# Revit family: 1f8d478efd5c45ef9d9ec268079f8082
name_source: partatom
category: Portes
units: mm (PartAtom-declared; Revit-internal decimal feet)

## family parameters
Couper avec des vides une fois chargée = Non
Hôte = Mur
Partagée = Non
Repère de localisation dans la pièce = Non
Toujours verticalement = Oui

## types (3) — shared parameters
Coefficient d'apport thermique solaire = 0.86
Coefficient de transfert thermique (U) = 5.5617 W/(m²·K)
Construction analytique = Grandes fenêtres à vitrage simple
Dormants = PVC - Blanc
Définir les propriétés thermiques par = Type schématique
Epaisseur = 40 mm  [stored 0.131234 ft]
Fermeture du mur = Par hôte
Fonction = Intérieur
Hauteur = 2100 mm
Hauteur de la poignée = 1000 mm  [stored 3.28084 ft]
ID de type de construction = SGL
Larg. Feuillure = 40 mm  [stored 0.131234 ft]
Opération = SingleSwingRight
Panneau = PVC - Blanc
Poignée = PVC - Blanc
Prof. Feuillure = 50 mm  [stored 0.164042 ft]
Transmission de la lumière visible = 0.9

## per-type parameters (varying)
| type | Largeur |
| 0.73m x 2.10m | 730 mm  [stored 2.39501 ft] |
| 0.83m x 2.10m | 830 mm  [stored 2.7231 ft] |
| 0.93m x 2.10m | 930 mm  [stored 3.05118 ft] |

note: [stored X ft] marks values corroborated as IEEE doubles in the binary element streams (Revit-internal decimal feet)
